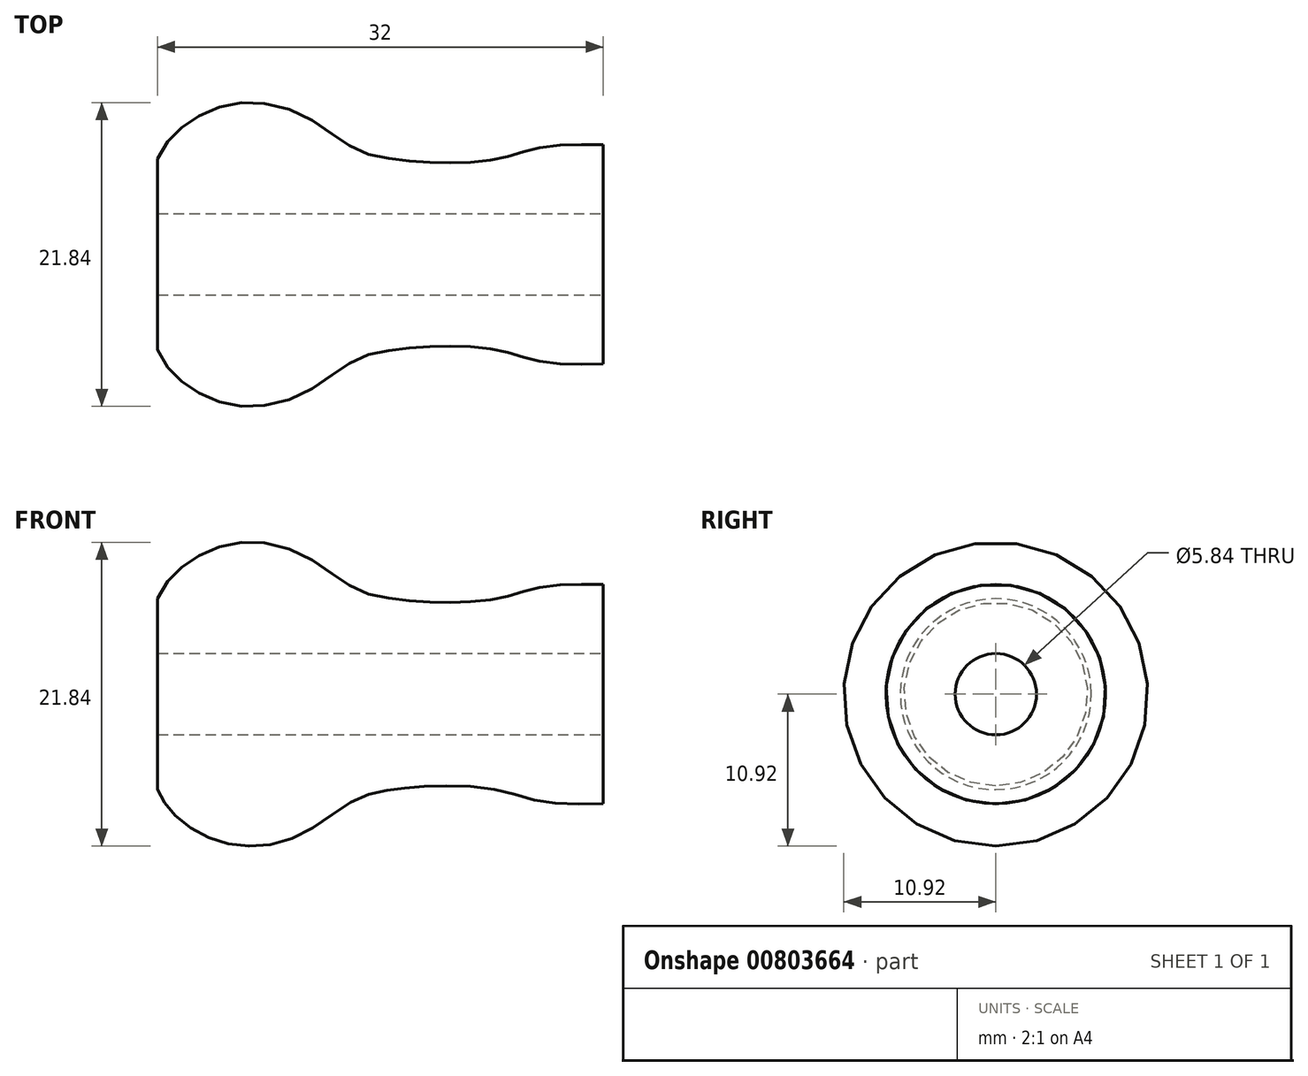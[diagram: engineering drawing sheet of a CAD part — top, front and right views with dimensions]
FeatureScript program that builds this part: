
annotation { "Feature Type Name" : "Feature", "Feature Type Description" : "" }
export const myFeature = defineFeature(function(context is Context, id is Id, definition is map)
    precondition{}
    {
        {
            var Q0;
            Q0=qCreatedBy(makeId("Front.planeOp"),FACE);
            var sketch = newSketch(context, id + "F0", { "sketchPlane" : qUnion([Q0])});
            skLineSegment(sketch, "E0", {"start": v(0, 0) * mm, "end": v(-32, 0) * mm});
            skLineSegment(sketch, "E1", {"start": v(-32, 0) * mm, "end": v(-32, 6.86) * mm});
            skLineSegment(sketch, "E2", {"start": v(0, 0) * mm, "end": v(0, 7.87) * mm});
            skLineSegment(sketch, "E3", {"start": v(-25.15, 0) * mm, "end": v(-25.15, 10.92) * mm, "construction": true});
            skLineSegment(sketch, "E4", {"start": v(-12.2, 0) * mm, "end": v(-12.2, 6.6) * mm, "construction": true});
            skFitSpline(sketch, "E5", {"points": [v(-32, 6.86) * mm, v(-30.96, 8.48) * mm, v(-28.43, 10.25) * mm, v(-25.15, 10.92) * mm, v(-21.35, 9.9) * mm, v(-17.82, 7.6) * mm, v(-15.16, 6.86) * mm, v(-12.2, 6.6) * mm, v(-7.68, 6.86) * mm, v(-4.38, 7.71) * mm, v(0, 7.87) * mm], "startDerivative": vector(11.17, 21.74) * mm, "endDerivative": vector(40.77, -0.94) * mm});
            skSolve(sketch);
        }
        {
            var Q0;
            Q0 = qSketchRegion(id + "F0", true);
            var Q1;
            Q1=sQuery(id+"F0.wireOp",EDGE,"E0");
            revolve(context, id + "F1", {"surfaceOperationType" : NewSurfaceOperationType.NEW, "entities" : qUnion([Q0]), "axis" : qUnion([Q1]), "revolveType" : RevolveType.FULL});
        }
        {
            var Q0;
            Q0=makeQuery(id+"F1.opRevolve","SWEPT_FACE",FACE,{"disambiguationData":[OSD([sQuery(id+"F0.wireOp",EDGE,"E1")])]});
            var sketch = newSketch(context, id + "F2", { "sketchPlane" : qUnion([Q0])});
            skCircle(sketch, "E6", {"center": v(0, 0) * mm, "radius": 2.92 * mm});
            skSolve(sketch);
        }
        {
            var Q0;
            Q0=makeQuery(id+"F2.imprint","IMPRINT",FACE,{"disambiguationData":[TD([[makeQuery(id+"F2.imprint","IMPRINT",EDGE,{"derivedFrom":sQuery(id+"F2.wireOp",EDGE,"E6")}),1.0]])]});
            extrude(context, id + "F3", {"entities" : qUnion([Q0]), "endBound" : BoundingType.SYMMETRIC, "depth" : 127 * mm, "offsetDistance" : 25.4 * mm});
        }
        {
            var Q0;
            Q0=makeQuery(id+"F3.opExtrude","SWEPT_BODY",BODY,{"disambiguationData":[OSD([sQuery(id+"F2.wireOp",EDGE,"E6")])]});
            var Q1;
            Q1=makeQuery(id+"F1.opRevolve","SWEPT_BODY",BODY,{"disambiguationData":[OSD([sQuery(id+"F0.wireOp",EDGE,"E0"),sQuery(id+"F0.wireOp",EDGE,"E1"),sQuery(id+"F0.wireOp",EDGE,"E2"),sQuery(id+"F0.wireOp",EDGE,"E5")])]});
            booleanBodies(context, id + "F4", {"operationType" : BooleanOperationType.SUBTRACTION, "tools" : qUnion([Q0]), "targets" : qUnion([Q1])});
        }
    });
